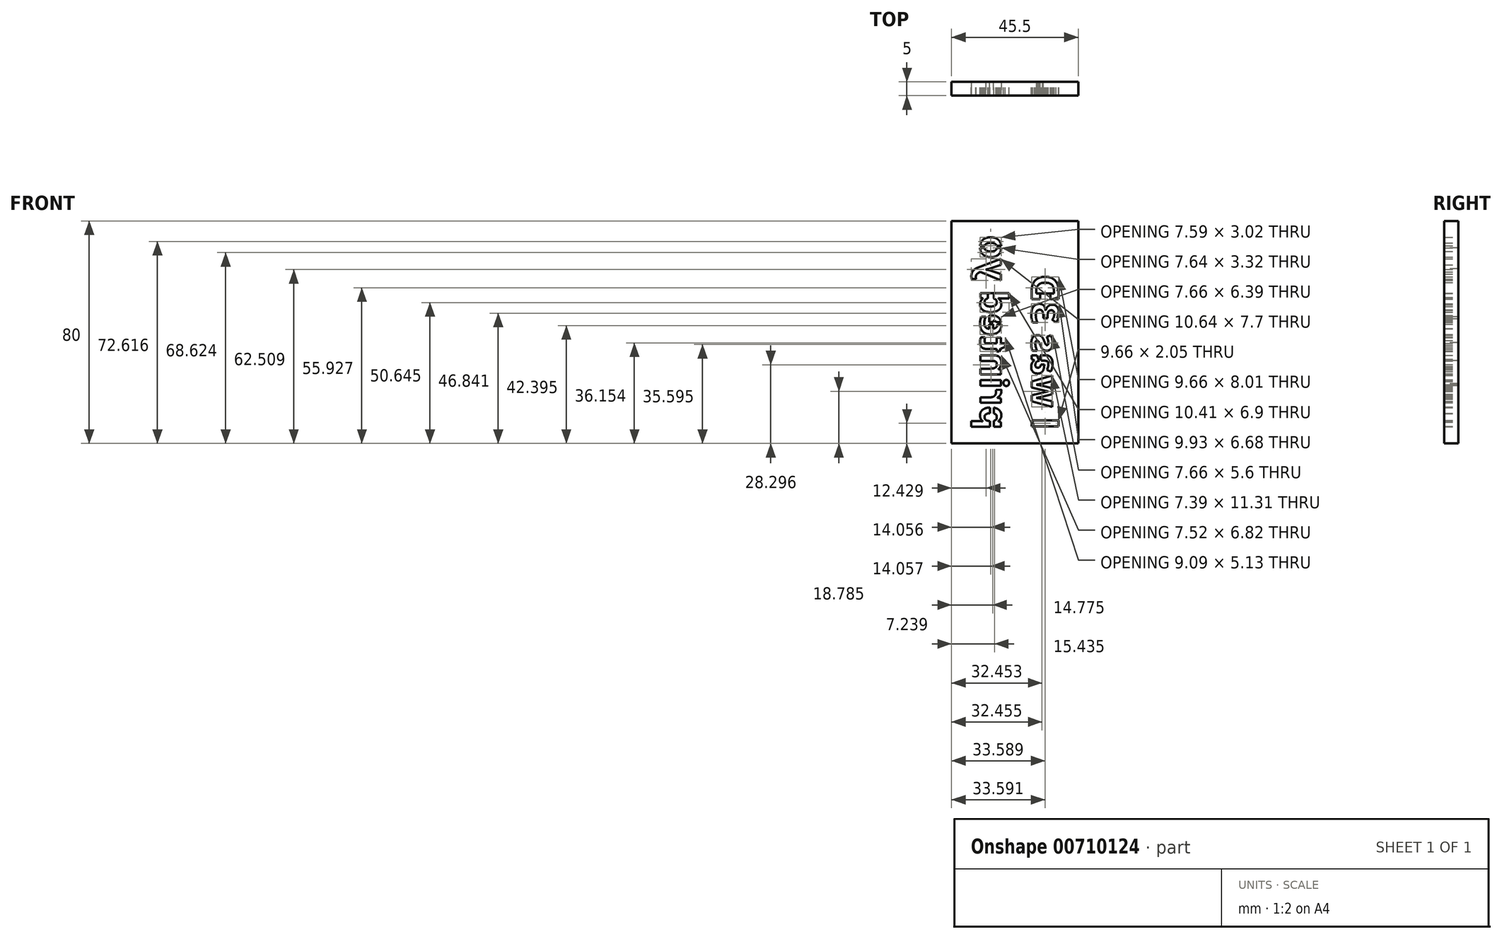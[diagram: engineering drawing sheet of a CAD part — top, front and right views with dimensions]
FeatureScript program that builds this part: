
annotation { "Feature Type Name" : "Feature", "Feature Type Description" : "" }
export const myFeature = defineFeature(function(context is Context, id is Id, definition is map)
    precondition{}
    {
        {
            var Q0;
            Q0=qCreatedBy(makeId("Top.planeOp"),FACE);
            var sketch = newSketch(context, id + "F0", { "sketchPlane" : qUnion([Q0])});
            skLineSegment(sketch, "E0.bottom", {"start": v(-22.75, 5) * mm, "end": v(22.75, 5) * mm});
            skLineSegment(sketch, "E0.top", {"start": v(-22.75, 0) * mm, "end": v(22.75, 0) * mm});
            skLineSegment(sketch, "E0.left", {"start": v(-22.75, 5) * mm, "end": v(-22.75, 0) * mm});
            skLineSegment(sketch, "E0.right", {"start": v(22.75, 5) * mm, "end": v(22.75, 0) * mm});
            skSolve(sketch);
        }
        {
            var Q0;
            Q0 = qSketchRegion(id + "F0", true);
            extrude(context, id + "F1", {"entities" : qUnion([Q0]), "depth" : 80 * mm, "offsetDistance" : 25 * mm});
        }
        {
            var Q0;
            Q0=makeQuery(id+"F1.opExtrude","SWEPT_FACE",FACE,{"disambiguationData":[OSD([sQuery(id+"F0.wireOp",EDGE,"E0.bottom")])]});
            var sketch = newSketch(context, id + "F2", { "sketchPlane" : qUnion([Q0])});
            skText(sketch, "E1", { "text": "I was 3D \nprinted yo", "fontName": "OpenSans-Bold.ttf"});
            const initialGuessF2  = {"E1": [-0.00601, 0.005, 0, 1, 0.00974]};
            skSetInitialGuess(sketch, initialGuessF2);
            skSolve(sketch);
        }
        {
            var Q0;
            Q0 = qSketchRegion(id + "F2", true);
            extrude(context, id + "F3", {"entities" : qUnion([Q0]), "operationType" : NewBodyOperationType.REMOVE, "oppositeDirection" : true, "depth" : 25 * mm, "offsetDistance" : 25 * mm});
        }
        {
            var Q0;
            {var subQ0=sQuery(id+"F0.wireOp",EDGE,"E0.left");var subQ3=sQuery(id+"F0.wireOp",EDGE,"E0.bottom");Q0=makeQuery(id+"F3.boolean.opBoolean","SPLIT",FACE,{"disambiguationData":[TD([makeQuery(id+"F1.opExtrude","SWEPT_FACE",FACE,{"disambiguationData":[OSD([subQ0])]})])],"derivedFrom":makeQuery(id+"F1.opExtrude","SWEPT_FACE",FACE,{"disambiguationData":[OSD([subQ3])]})});}
            var sketch = newSketch(context, id + "F4", { "sketchPlane" : qUnion([Q0])});
            skLineSegment(sketch, "E2.bottom", {"start": v(-12.73, 51.92) * mm, "end": v(-9.12, 51.92) * mm});
            skLineSegment(sketch, "E2.top", {"start": v(-12.73, 53.97) * mm, "end": v(-9.12, 53.97) * mm});
            skLineSegment(sketch, "E2.left", {"start": v(-12.73, 51.92) * mm, "end": v(-12.73, 53.97) * mm});
            skLineSegment(sketch, "E2.right", {"start": v(-9.12, 51.92) * mm, "end": v(-9.12, 53.97) * mm});
            skLineSegment(sketch, "E3.bottom", {"start": v(7.59, 54.1) * mm, "end": v(9.76, 54.1) * mm});
            skLineSegment(sketch, "E3.top", {"start": v(7.59, 51.52) * mm, "end": v(9.76, 51.52) * mm});
            skLineSegment(sketch, "E3.left", {"start": v(7.59, 54.1) * mm, "end": v(7.59, 51.52) * mm});
            skLineSegment(sketch, "E3.right", {"start": v(9.76, 54.1) * mm, "end": v(9.76, 51.52) * mm});
            skLineSegment(sketch, "E4.bottom", {"start": v(4.87, 70.27) * mm, "end": v(12.52, 70.27) * mm});
            skLineSegment(sketch, "E4.top", {"start": v(4.87, 71.1) * mm, "end": v(12.52, 71.1) * mm});
            skLineSegment(sketch, "E4.left", {"start": v(4.87, 70.27) * mm, "end": v(4.87, 71.1) * mm});
            skLineSegment(sketch, "E4.right", {"start": v(12.52, 70.27) * mm, "end": v(12.52, 71.1) * mm});
            skLineSegment(sketch, "E5.bottom", {"start": v(4, 42.8) * mm, "end": v(9.2, 42.8) * mm});
            skLineSegment(sketch, "E5.top", {"start": v(4, 43.62) * mm, "end": v(9.2, 43.62) * mm});
            skLineSegment(sketch, "E5.left", {"start": v(4, 42.8) * mm, "end": v(4, 43.62) * mm});
            skLineSegment(sketch, "E5.right", {"start": v(9.2, 42.8) * mm, "end": v(9.2, 43.62) * mm});
            skLineSegment(sketch, "E6.bottom", {"start": v(7.6, 6.06) * mm, "end": v(8.99, 6.06) * mm});
            skLineSegment(sketch, "E6.top", {"start": v(7.6, 12.95) * mm, "end": v(8.99, 12.95) * mm});
            skLineSegment(sketch, "E6.left", {"start": v(7.6, 6.06) * mm, "end": v(7.6, 12.95) * mm});
            skLineSegment(sketch, "E6.right", {"start": v(8.99, 6.06) * mm, "end": v(8.99, 12.95) * mm});
            skLineSegment(sketch, "E7", {"start": v(-10.6, 29.73) * mm, "end": v(-9.43, 29.73) * mm});
            skLineSegment(sketch, "E8", {"start": v(-9.43, 29.73) * mm, "end": v(-9.36, 28.44) * mm});
            skLineSegment(sketch, "E9", {"start": v(-9.36, 28.44) * mm, "end": v(-10.57, 28.44) * mm});
            skLineSegment(sketch, "E10", {"start": v(-10.57, 28.44) * mm, "end": v(-10.6, 29.73) * mm});
            skLineSegment(sketch, "E11", {"start": v(-9.43, 29.73) * mm, "end": v(-9.12, 31.73) * mm});
            skLineSegment(sketch, "E12", {"start": v(-9.12, 31.73) * mm, "end": v(-7.97, 31.73) * mm});
            skLineSegment(sketch, "E13", {"start": v(-7.97, 31.73) * mm, "end": v(-8.73, 29.73) * mm});
            skLineSegment(sketch, "E14", {"start": v(-8.73, 29.73) * mm, "end": v(-9.43, 29.73) * mm});
            skSolve(sketch);
        }
        {
            var Q0;
            Q0 = qSketchRegion(id + "F4", true);
            extrude(context, id + "F5", {"entities" : qUnion([Q0]), "operationType" : NewBodyOperationType.ADD, "oppositeDirection" : true, "depth" : 5 * mm, "offsetDistance" : 25 * mm});
        }
    });
